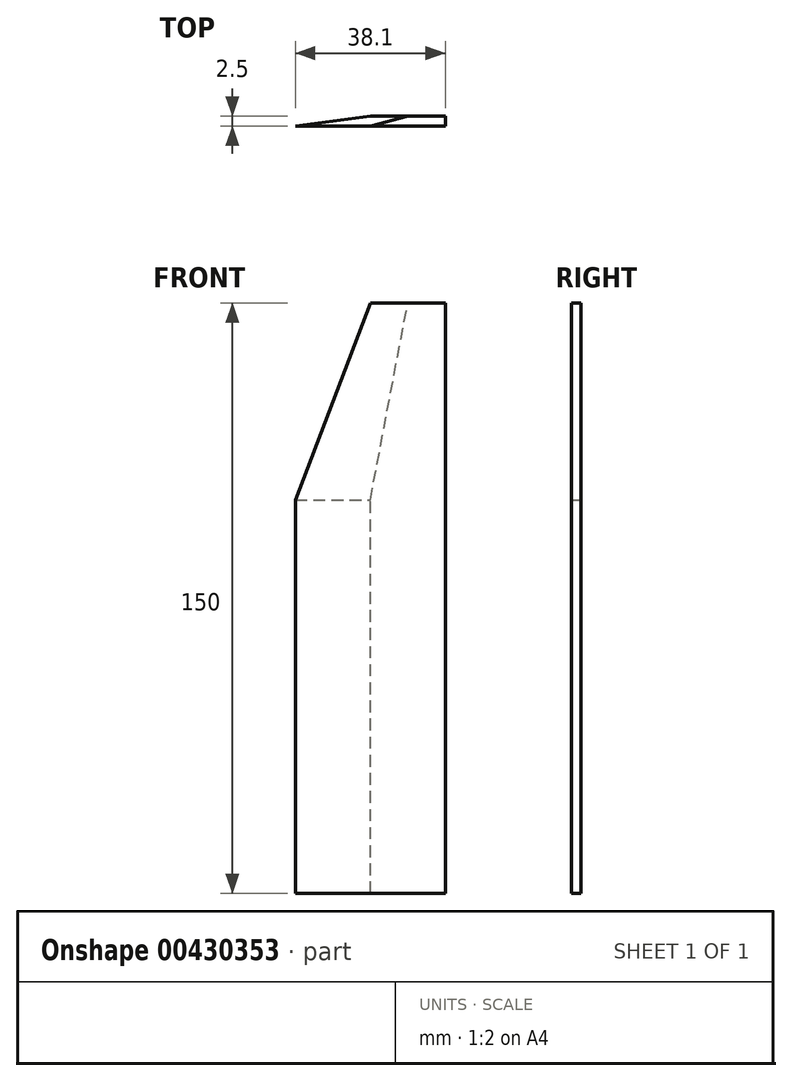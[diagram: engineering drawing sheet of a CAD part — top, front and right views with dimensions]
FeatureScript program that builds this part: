
annotation { "Feature Type Name" : "Feature", "Feature Type Description" : "" }
export const myFeature = defineFeature(function(context is Context, id is Id, definition is map)
    precondition{}
    {
        {
            var Q0;
            Q0=qCreatedBy(makeId("Top.planeOp"),FACE);
            var sketch = newSketch(context, id + "F0", { "sketchPlane" : qUnion([Q0])});
            skLineSegment(sketch, "E0.bottom", {"start": v(19.05, -1.25) * mm, "end": v(-19.05, -1.25) * mm});
            skLineSegment(sketch, "E0.top", {"start": v(19.05, 1.25) * mm, "end": v(0, 1.25) * mm});
            skLineSegment(sketch, "E0.left", {"start": v(19.05, -1.25) * mm, "end": v(19.05, 1.25) * mm});
            skPoint(sketch, "E0.middle", {"position": v(0, 0) * mm});
            skLineSegment(sketch, "E1", {"start": v(-19.05, -1.25) * mm, "end": v(0, 1.25) * mm});
            skPoint(sketch, "E2.orphan", {"position": v(-19.05, 1.25) * mm});
            skSolve(sketch);
        }
        {
            var Q0;
            Q0=qCreatedBy(makeId("Top.planeOp"),FACE);
            cPlane(context, id + "F1", {"entities" : qUnion([Q0]), "cplaneType" : CPlaneType.OFFSET, "offset" : 100 * mm, "width" : 152.4 * mm, "height" : 152.4 * mm});
        }
        {
            var Q0;
            Q0=qCreatedBy(id+"F1.planeOp",FACE);
            var sketch = newSketch(context, id + "F2", { "sketchPlane" : qUnion([Q0])});
            skLineSegment(sketch, "E3.bottom", {"start": v(19.05, -1.25) * mm, "end": v(-19.05, -1.25) * mm});
            skLineSegment(sketch, "E3.top", {"start": v(19.05, 1.25) * mm, "end": v(0, 1.25) * mm});
            skLineSegment(sketch, "E3.left", {"start": v(19.05, -1.25) * mm, "end": v(19.05, 1.25) * mm});
            skPoint(sketch, "E3.middle", {"position": v(0, 0) * mm});
            skLineSegment(sketch, "E4", {"start": v(-19.05, -1.25) * mm, "end": v(0, 1.25) * mm});
            skPoint(sketch, "E3.right.end.orphan", {"position": v(-19.05, 1.25) * mm});
            skSolve(sketch);
        }
        {
            var Q0;
            Q0=qCreatedBy(id+"F1.planeOp",FACE);
            cPlane(context, id + "F3", {"entities" : qUnion([Q0]), "cplaneType" : CPlaneType.OFFSET, "offset" : 50 * mm, "width" : 152.4 * mm, "height" : 152.4 * mm});
        }
        {
            var Q0;
            Q0=qCreatedBy(id+"F3.planeOp",FACE);
            var sketch = newSketch(context, id + "F4", { "sketchPlane" : qUnion([Q0])});
            skLineSegment(sketch, "E5.bottom", {"start": v(19.05, -1.25) * mm, "end": v(0, -1.25) * mm});
            skLineSegment(sketch, "E5.top", {"start": v(19.05, 1.25) * mm, "end": v(9.53, 1.25) * mm});
            skLineSegment(sketch, "E5.left", {"start": v(19.05, -1.25) * mm, "end": v(19.05, 1.25) * mm});
            skPoint(sketch, "E5.middle", {"position": v(0, 0) * mm});
            skLineSegment(sketch, "E6", {"start": v(9.53, 1.25) * mm, "end": v(19.05, 1.25) * mm});
            skLineSegment(sketch, "E7", {"start": v(0, -1.25) * mm, "end": v(9.53, 1.25) * mm});
            skPoint(sketch, "E5.right.start.orphan", {"position": v(-19.05, -1.25) * mm});
            skPoint(sketch, "E8.orphan", {"position": v(-19.05, 1.25) * mm});
            skPoint(sketch, "E9.orphan", {"position": v(0, 1.25) * mm});
            skSolve(sketch);
        }
        {
            var Q0;
            Q0=qSketchRegion(id+"F0",true);
            var Q1;
            Q1=qSketchRegion(id+"F2",true);
            loft(context, id + "F5", {"sheetProfilesArray" : [{ "sheetProfileEntities" : qUnion([Q0]) }, { "sheetProfileEntities" : qUnion([Q1]) }]});
        }
        {
            var Q1;
            Q1=qSketchRegion(id+"F2",true);
            var Q2;
            Q2=qSketchRegion(id+"F4",true);
            loft(context, id + "F6", {"operationType" : NewBodyOperationType.ADD, "sheetProfilesArray" : [{ "sheetProfileEntities" : qUnion([Q1]) }, { "sheetProfileEntities" : qUnion([Q2]) }]});
        }
    });
